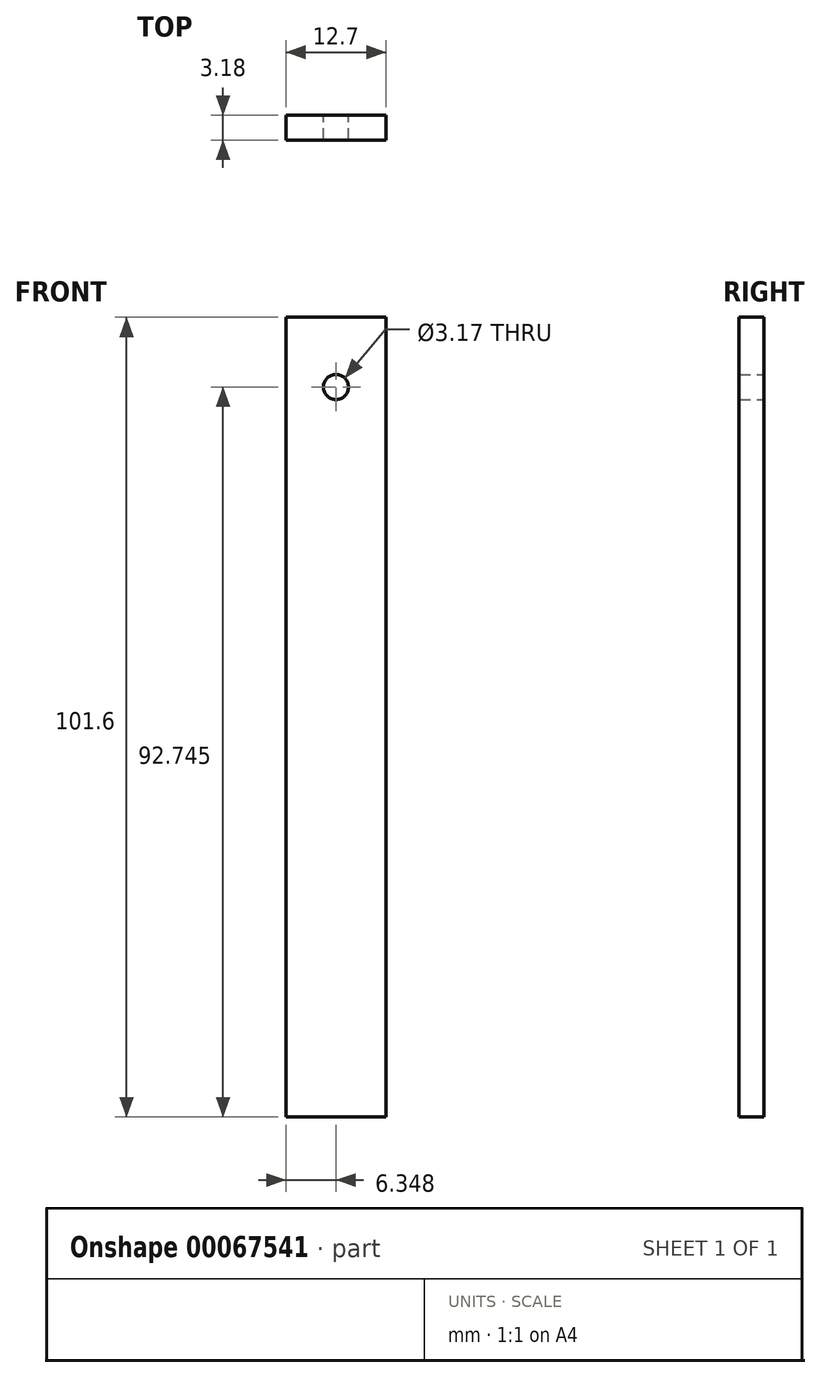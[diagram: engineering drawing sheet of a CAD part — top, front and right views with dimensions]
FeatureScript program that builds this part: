
annotation { "Feature Type Name" : "Feature", "Feature Type Description" : "" }
export const myFeature = defineFeature(function(context is Context, id is Id, definition is map)
    precondition{}
    {
        {
            var Q0;
            Q0=qCreatedBy(makeId("Front.planeOp"),FACE);
            var sketch = newSketch(context, id + "F0", { "sketchPlane" : qUnion([Q0])});
            skLineSegment(sketch, "E0.bottom", {"start": v(-29.2, -165.9) * mm, "end": v(-16.5, -165.9) * mm});
            skLineSegment(sketch, "E0.top", {"start": v(-29.2, -267.5) * mm, "end": v(-16.5, -267.5) * mm});
            skLineSegment(sketch, "E0.left", {"start": v(-29.2, -165.9) * mm, "end": v(-29.2, -267.5) * mm});
            skLineSegment(sketch, "E0.right", {"start": v(-16.5, -165.9) * mm, "end": v(-16.5, -267.5) * mm});
            skCircle(sketch, "E1", {"center": v(-22.85, -174.75) * mm, "radius": 1.59 * mm});
            skPoint(sketch, "E1.centerSnap0", {"position": v(-22.85, -165.9) * mm});
            skSolve(sketch);
        }
        {
            var Q0;
            Q0=makeQuery(id+"F0.imprint","IMPRINT",FACE,{"disambiguationData":[TD([[makeQuery(id+"F0.imprint","IMPRINT",EDGE,{"derivedFrom":sQuery(id+"F0.wireOp",EDGE,"E0.bottom")}),-1.0]])]});
            extrude(context, id + "F1", {"entities" : qUnion([Q0]), "depth" : 3.17 * mm});
        }
    });
